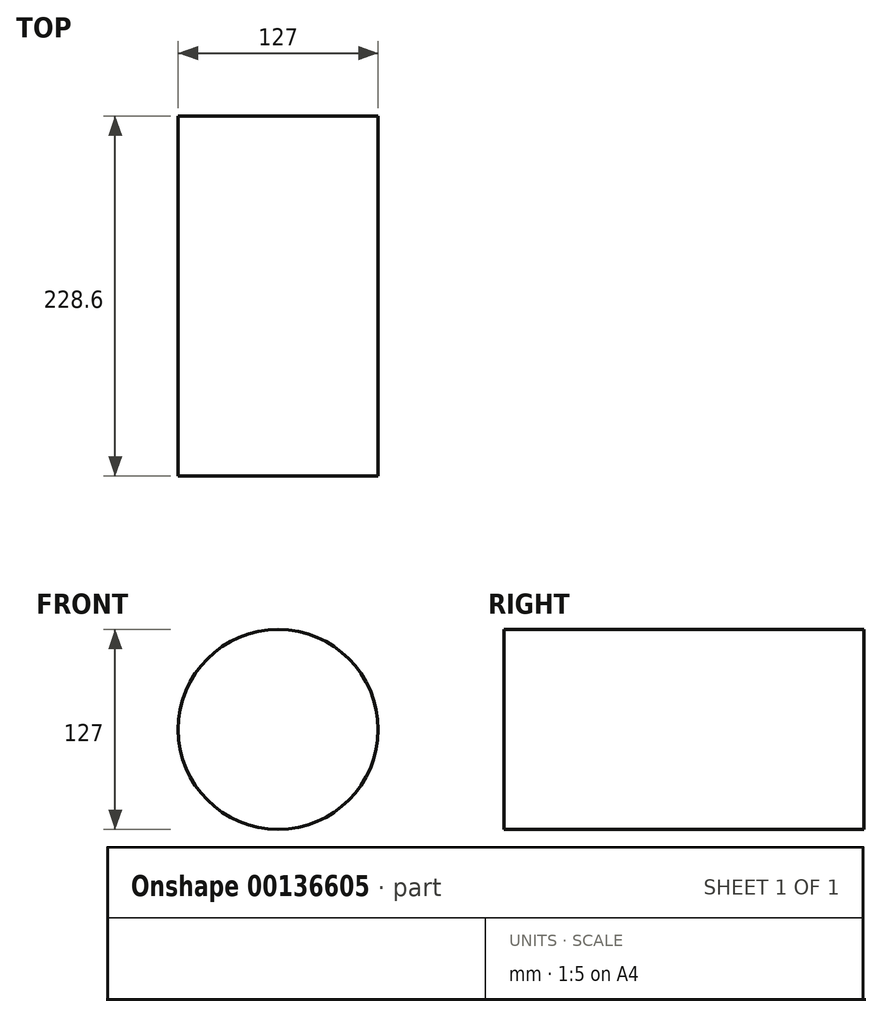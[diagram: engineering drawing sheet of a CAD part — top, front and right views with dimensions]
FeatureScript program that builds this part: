
annotation { "Feature Type Name" : "Feature", "Feature Type Description" : "" }
export const myFeature = defineFeature(function(context is Context, id is Id, definition is map)
    precondition{}
    {
        {
            var Q0;
            Q0=qCreatedBy(makeId("Front.planeOp"),FACE);
            var sketch = newSketch(context, id + "F0", { "sketchPlane" : qUnion([Q0])});
            skCircle(sketch, "E0", {"center": v(0, 0) * mm, "radius": 63.5 * mm});
            skSolve(sketch);
        }
        {
            var Q0;
            Q0 = qSketchRegion(id + "F0", true);
            extrude(context, id + "F1", {"entities" : qUnion([Q0]), "depth" : 228.6 * mm, "symmetric" : true});
        }
    });
